# Revit family: GRIFO LAVABO INGO PLUS
name_source: partatom
category: Aparatos sanitarios
revit_build: Autodesk Revit 2015 (Build: 20140223_1515(x64)
units: mm (PartAtom-declared; Revit-internal decimal feet)

## types (1)
- 7155000
    Comentarios de tipo = ◦Grifo monomando de lavabo
◦Acabado Cromo
◦Disponible sin Desagüe automático
◦Cartucho con discos cerámicos de diámetro 40 mm
◦Tubos de alimentación flexibles 3/8" y longitud 35 cm.
    Conexión AC = Sí
    Conexión AF = Sí
    Código de montaje = C1030220
    Descripción = Grifo monomando de lavabo. La serie INGO PLUS es un nuevo funcional monomando de dimensiones reducidas que destaca por sus líneas rectas que le diferencian de un simple grifo Tradicional. Su estética robusta es a su vez elegante y limpia haciendo de este grifo un monomando moderno, funcional y proporcionado especialmente diseñado para espacios pequeños.
    Elevación por defecto = 1219 mm
    Fabricante = PRESTO IBÉRICA
    Imagen de tipo = <Ninguno>
    Material = LATON CROMADO
    Modelo = INGO PLUS
    REFERENCIA = 7155000
    Teléfono = (+34) 915 782 575
    URL = http://www.griferiasgalindo.com
